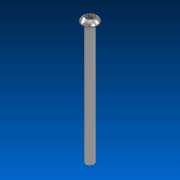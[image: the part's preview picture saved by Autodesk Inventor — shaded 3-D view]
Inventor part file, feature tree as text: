
AUTODESK INVENTOR PART (.ipt)
format: ipt  version: 2022.2 (Build 262287000, 287)  size: 159,744 bytes
history: native  units: in
note: dims shown in document units (in); Inventor stores cm internally (conversion verified against a paired STEP export)
features: direct_edit x1, chamfer x1, move_body x1
ambient origin geometry x8: Origin, YZ Plane, XZ Plane, XY Plane, X Axis, Y Axis, Z Axis, Center Point
bodies: Solid1 (feature_tree)
feature tree (3):
  direct_edit  "Direct Edit1"
  chamfer  "Chamfer2"  Distance=0.25in
  move_body  "Move1"
